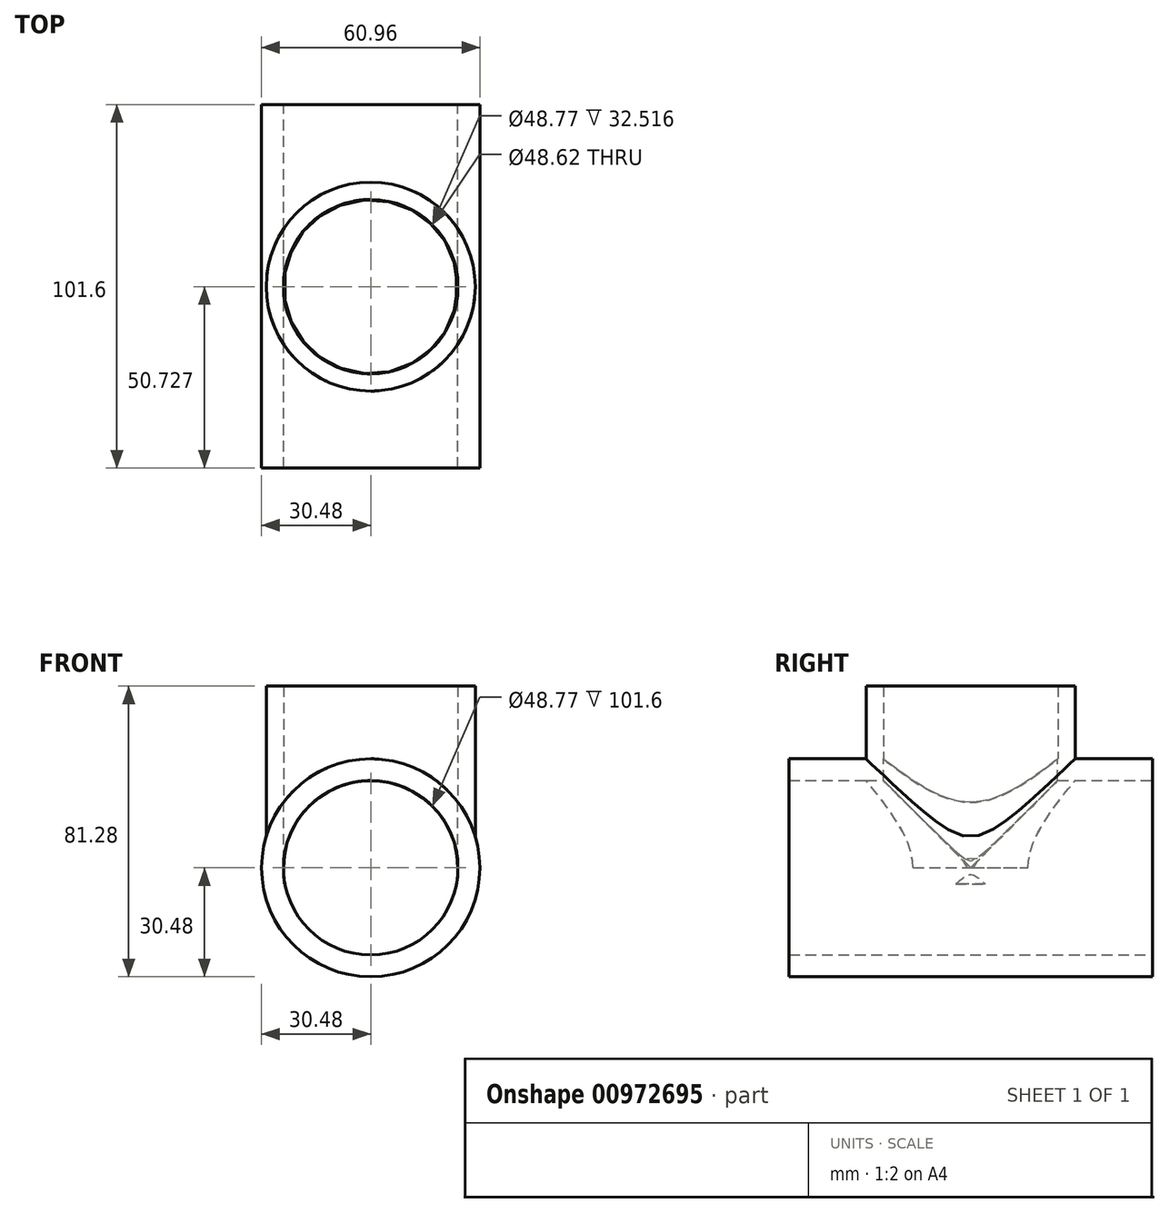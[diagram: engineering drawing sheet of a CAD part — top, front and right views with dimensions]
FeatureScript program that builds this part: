
annotation { "Feature Type Name" : "Feature", "Feature Type Description" : "" }
export const myFeature = defineFeature(function(context is Context, id is Id, definition is map)
    precondition{}
    {
        {
            var Q0;
            Q0=qCreatedBy(makeId("Front.planeOp"),FACE);
            var sketch = newSketch(context, id + "F0", { "sketchPlane" : qUnion([Q0])});
            skCircle(sketch, "E0", {"center": v(0, 0) * mm, "radius": 24.38 * mm});
            skCircle(sketch, "E1", {"center": v(0, 0) * mm, "radius": 30.48 * mm});
            skSolve(sketch);
        }
        {
            var Q0;
            Q0 = qSketchRegion(id + "F0", true);
            extrude(context, id + "F1", {"entities" : qUnion([Q0]), "depth" : 101.6 * mm, "offsetDistance" : 25.4 * mm});
        }
        {
            var Q0;
            Q0=qCreatedBy(makeId("Top.planeOp"),FACE);
            var sketch = newSketch(context, id + "F2", { "sketchPlane" : qUnion([Q0])});
            skLineSegment(sketch, "E2", {"start": v(0, 0) * mm, "end": v(0, -101.75) * mm});
            skCircle(sketch, "E3", {"center": v(0, -50.87) * mm, "radius": 24.38 * mm});
            skCircle(sketch, "E4", {"center": v(0, -50.87) * mm, "radius": 29.21 * mm});
            skSolve(sketch);
        }
        {
            var Q0;
            Q0 = qSketchRegion(id + "F2", true);
            extrude(context, id + "F3", {"entities" : qUnion([Q0]), "operationType" : NewBodyOperationType.ADD, "depth" : 50.8 * mm, "offsetDistance" : 25.4 * mm});
        }
        {
            var Q0;
            Q0=makeQuery(id+"F3.opExtrude","CAP_FACE",FACE,{"disambiguationData":[OSD([sQuery(id+"F2.wireOp",EDGE,"E3"),sQuery(id+"F2.wireOp",EDGE,"E4")])],"isStart":false});
            var sketch = newSketch(context, id + "F4", { "sketchPlane" : qUnion([Q0])});
            skCircle(sketch, "E5", {"center": v(0, -50.87) * mm, "radius": 24.31 * mm});
            skSolve(sketch);
        }
        {
            var Q0;
            Q0=makeQuery(id+"F4.imprint","IMPRINT",FACE,{"disambiguationData":[TD([[makeQuery(id+"F4.imprint","IMPRINT",EDGE,{"derivedFrom":sQuery(id+"F4.wireOp",EDGE,"E5")}),1.0]])]});
            extrude(context, id + "F5", {"entities" : qUnion([Q0]), "operationType" : NewBodyOperationType.REMOVE, "oppositeDirection" : true, "depth" : 55.37 * mm, "offsetDistance" : 25.4 * mm});
        }
        {
            var Q0;
            Q0=makeQuery(id+"F1.opExtrude","CAP_FACE",FACE,{"disambiguationData":[OSD([sQuery(id+"F0.wireOp",EDGE,"E0"),sQuery(id+"F0.wireOp",EDGE,"E1")])],"isStart":true});
            var sketch = newSketch(context, id + "F6", { "sketchPlane" : qUnion([Q0])});
            skCircle(sketch, "E6", {"center": v(0, 0) * mm, "radius": 24.37 * mm});
            skSolve(sketch);
        }
        {
            var Q0;
            Q0=makeQuery(id+"F6.imprint","IMPRINT",FACE,{"disambiguationData":[TD([[makeQuery(id+"F6.imprint","IMPRINT",EDGE,{"derivedFrom":sQuery(id+"F6.wireOp",EDGE,"E6")}),1.0]])]});
            extrude(context, id + "F7", {"entities" : qUnion([Q0]), "operationType" : NewBodyOperationType.REMOVE, "oppositeDirection" : true, "depth" : 105.66 * mm, "offsetDistance" : 25.4 * mm});
        }
    });
